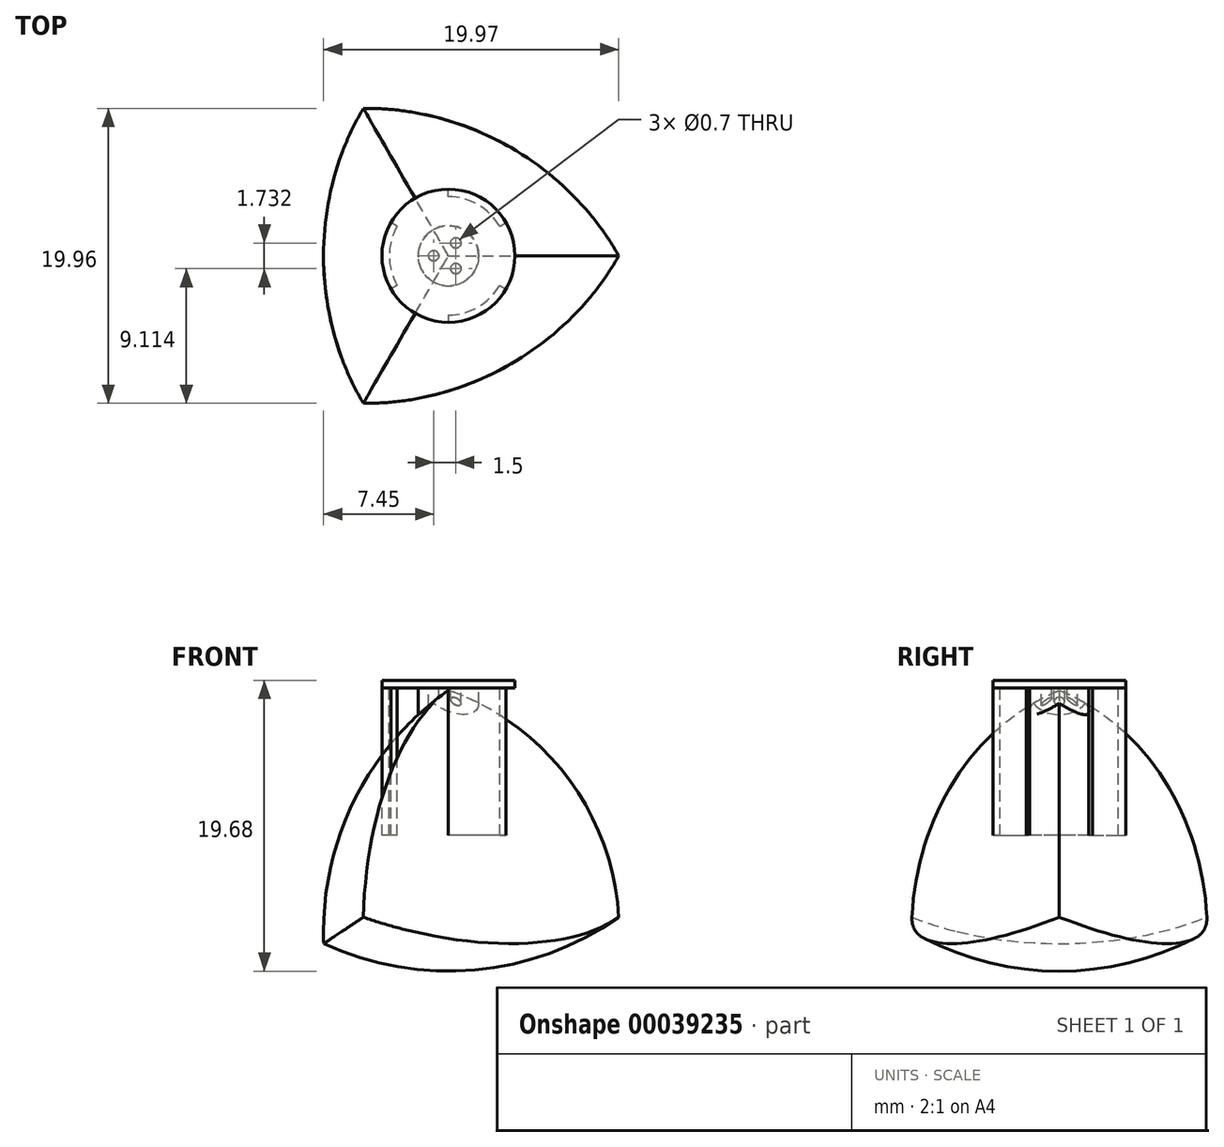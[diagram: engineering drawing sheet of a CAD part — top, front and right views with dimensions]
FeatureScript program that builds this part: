
annotation { "Feature Type Name" : "Feature", "Feature Type Description" : "" }
export const myFeature = defineFeature(function(context is Context, id is Id, definition is map)
    precondition{}
    {
        {
            var Q0;
            Q0=qCreatedBy(makeId("Top.planeOp"),FACE);
            var sketch = newSketch(context, id + "F0", { "sketchPlane" : qUnion([Q0])});
            skCircle(sketch, "E0", {"center": v(11.55, 0) * mm, "radius": 20 * mm});
            skCircle(sketch, "E1.1.0", {"center": v(-5.77, 10) * mm, "radius": 20 * mm});
            skCircle(sketch, "E1.2.0", {"center": v(-5.77, -10) * mm, "radius": 20 * mm});
            skPoint(sketch, "E1.center", {"position": v(0, 0) * mm});
            skLineSegment(sketch, "E2", {"start": v(31.55, 0) * mm, "end": v(-8.45, 0) * mm});
            skLineSegment(sketch, "E3", {"start": v(0, 0) * mm, "end": v(-5.77, -10) * mm});
            skLineSegment(sketch, "E4", {"start": v(-5.77, -10) * mm, "end": v(-15.77, -27.32) * mm});
            skLineSegment(sketch, "E5", {"start": v(0, 0) * mm, "end": v(4.23, 7.32) * mm});
            skLineSegment(sketch, "E6", {"start": v(-5.77, 10) * mm, "end": v(0, 0) * mm});
            skLineSegment(sketch, "E7", {"start": v(0, 0) * mm, "end": v(4.23, -7.32) * mm});
            skLineSegment(sketch, "E8", {"start": v(-5.77, 10) * mm, "end": v(-15.77, 27.32) * mm});
            skSolve(sketch);
        }
        {
            var Q0;
            {var subQ1=sQuery(id+"F0.wireOp",EDGE,"E2");var subQ3=sQuery(id+"F0.wireOp",EDGE,"E0");var subQ5=makeQuery(id+"F0.imprint","INTERSECT",VERTEX,{"disambiguationData":[OD(0.0)],"derivedFrom":[subQ3,subQ1]});Q0=makeQuery(id+"F0.imprint","IMPRINT",FACE,{"disambiguationData":[TD([[makeQuery(id+"F0.imprint","IMPRINT",EDGE,{"disambiguationData":[TD([[subQ5,-1.0]])],"derivedFrom":subQ3}),1.0]])]});}
            var Q1;
            {var subQ1=sQuery(id+"F0.wireOp",EDGE,"E0");var subQ4=sQuery(id+"F0.wireOp",EDGE,"E1.1.0");var subQ6=makeQuery(id+"F0.imprint","INTERSECT",VERTEX,{"derivedFrom":[subQ1,subQ4]});Q1=makeQuery(id+"F0.imprint","IMPRINT",FACE,{"disambiguationData":[TD([[makeQuery(id+"F0.imprint","IMPRINT",EDGE,{"disambiguationData":[TD([[subQ6,1.0]])],"derivedFrom":subQ4}),1.0]])]});}
            var Q2;
            {var subQ1=sQuery(id+"F0.wireOp",EDGE,"E5");Q2=makeQuery(id+"F0.imprint","IMPRINT",FACE,{"disambiguationData":[TD([[makeQuery(id+"F0.imprint","IMPRINT",EDGE,{"derivedFrom":subQ1}),1.0]])]});}
            var Q3;
            {var subQ0=sQuery(id+"F0.wireOp",EDGE,"E5");Q3=makeQuery(id+"F0.imprint","IMPRINT",FACE,{"disambiguationData":[TD([[makeQuery(id+"F0.imprint","IMPRINT",EDGE,{"derivedFrom":subQ0}),-1.0]])]});}
            var Q4;
            {var subQ0=sQuery(id+"F0.wireOp",EDGE,"E6");Q4=makeQuery(id+"F0.imprint","IMPRINT",FACE,{"disambiguationData":[TD([[makeQuery(id+"F0.imprint","IMPRINT",EDGE,{"derivedFrom":subQ0}),-1.0]])]});}
            var Q5;
            Q5=sQuery(id+"F0.wireOp",EDGE,"E2");
            revolve(context, id + "F1", {"entities" : qUnion([Q0, Q1, Q2, Q3, Q4]), "axis" : qUnion([Q5]), "revolveType" : RevolveType.FULL});
        }
        {
            var Q0;
            {var subQ1=sQuery(id+"F0.wireOp",EDGE,"E0");var subQ4=sQuery(id+"F0.wireOp",EDGE,"E1.1.0");var subQ6=makeQuery(id+"F0.imprint","INTERSECT",VERTEX,{"derivedFrom":[subQ1,subQ4]});Q0=makeQuery(id+"F0.imprint","IMPRINT",FACE,{"disambiguationData":[TD([[makeQuery(id+"F0.imprint","IMPRINT",EDGE,{"disambiguationData":[TD([[subQ6,1.0]])],"derivedFrom":subQ4}),1.0]])]});}
            var Q1;
            {var subQ0=sQuery(id+"F0.wireOp",EDGE,"E5");Q1=makeQuery(id+"F0.imprint","IMPRINT",FACE,{"disambiguationData":[TD([[makeQuery(id+"F0.imprint","IMPRINT",EDGE,{"derivedFrom":subQ0}),-1.0]])]});}
            var Q2;
            {var subQ1=sQuery(id+"F0.wireOp",EDGE,"E5");Q2=makeQuery(id+"F0.imprint","IMPRINT",FACE,{"disambiguationData":[TD([[makeQuery(id+"F0.imprint","IMPRINT",EDGE,{"derivedFrom":subQ1}),1.0]])]});}
            var Q3;
            {var subQ3=sQuery(id+"F0.wireOp",EDGE,"E7");Q3=makeQuery(id+"F0.imprint","IMPRINT",FACE,{"disambiguationData":[TD([[makeQuery(id+"F0.imprint","IMPRINT",EDGE,{"derivedFrom":subQ3}),1.0]])]});}
            var Q4;
            {var subQ0=sQuery(id+"F0.wireOp",EDGE,"E8");Q4=makeQuery(id+"F0.imprint","IMPRINT",FACE,{"disambiguationData":[TD([[makeQuery(id+"F0.imprint","IMPRINT",EDGE,{"derivedFrom":subQ0}),-1.0]])]});}
            var Q5;
            Q5=sQuery(id+"F0.wireOp",EDGE,"E8");
            revolve(context, id + "F2", {"entities" : qUnion([Q0, Q1, Q2, Q3, Q4]), "axis" : qUnion([Q5]), "revolveType" : RevolveType.FULL});
        }
        {
            var Q0;
            {var subQ3=sQuery(id+"F0.wireOp",EDGE,"E4");Q0=makeQuery(id+"F0.imprint","IMPRINT",FACE,{"disambiguationData":[TD([[makeQuery(id+"F0.imprint","IMPRINT",EDGE,{"derivedFrom":subQ3}),-1.0]])]});}
            var Q1;
            {var subQ3=sQuery(id+"F0.wireOp",EDGE,"E0");var subQ6=makeQuery(id+"F0.imprint","INTERSECT",VERTEX,{"disambiguationData":[OD(1.0)],"derivedFrom":[subQ3,sQuery(id+"F0.wireOp",EDGE,"E2")]});Q1=makeQuery(id+"F0.imprint","IMPRINT",FACE,{"disambiguationData":[TD([[makeQuery(id+"F0.imprint","IMPRINT",EDGE,{"disambiguationData":[TD([[subQ6,1.0]])],"derivedFrom":subQ3}),-1.0]])]});}
            var Q2;
            {var subQ0=sQuery(id+"F0.wireOp",EDGE,"E3");Q2=makeQuery(id+"F0.imprint","IMPRINT",FACE,{"disambiguationData":[TD([[makeQuery(id+"F0.imprint","IMPRINT",EDGE,{"derivedFrom":subQ0}),-1.0]])]});}
            var Q3;
            {var subQ0=sQuery(id+"F0.wireOp",EDGE,"E6");Q3=makeQuery(id+"F0.imprint","IMPRINT",FACE,{"disambiguationData":[TD([[makeQuery(id+"F0.imprint","IMPRINT",EDGE,{"derivedFrom":subQ0}),-1.0]])]});}
            var Q4;
            {var subQ1=sQuery(id+"F0.wireOp",EDGE,"E5");Q4=makeQuery(id+"F0.imprint","IMPRINT",FACE,{"disambiguationData":[TD([[makeQuery(id+"F0.imprint","IMPRINT",EDGE,{"derivedFrom":subQ1}),1.0]])]});}
            var Q5;
            Q5=sQuery(id+"F0.wireOp",EDGE,"E4");
            revolve(context, id + "F3", {"entities" : qUnion([Q0, Q1, Q2, Q3, Q4]), "axis" : qUnion([Q5]), "revolveType" : RevolveType.FULL});
        }
        {
            var Q0;
            Q0=qCreatedBy(makeId("Top.planeOp"),FACE);
            cPlane(context, id + "F4", {"entities" : qUnion([Q0]), "cplaneType" : CPlaneType.OFFSET, "offset" : 17.32 * mm, "width" : 150 * mm, "height" : 150 * mm});
        }
        {
            var Q0;
            Q0=qCreatedBy(id+"F4.planeOp",FACE);
            var sketch = newSketch(context, id + "F5", { "sketchPlane" : qUnion([Q0])});
            skCircle(sketch, "E9", {"center": v(0, 0) * mm, "radius": 20 * mm});
            skLineSegment(sketch, "E10", {"start": v(20, 0) * mm, "end": v(-20, 0) * mm});
            skSolve(sketch);
        }
        {
            var Q0;
            {var subQ0=sQuery(id+"F5.wireOp",EDGE,"E10");Q0=makeQuery(id+"F5.imprint","IMPRINT",FACE,{"disambiguationData":[TD([[makeQuery(id+"F5.imprint","IMPRINT",EDGE,{"derivedFrom":subQ0}),-1.0]])]});}
            var Q1;
            Q1=sQuery(id+"F5.wireOp",EDGE,"E10");
            revolve(context, id + "F6", {"entities" : qUnion([Q0]), "axis" : qUnion([Q1]), "revolveType" : RevolveType.FULL});
        }
        {
            var Q0;
            Q0=makeQuery(id+"F6.opRevolve","SWEPT_BODY",BODY,{"disambiguationData":[OSD([sQuery(id+"F5.wireOp",EDGE,"E9"),sQuery(id+"F5.wireOp",EDGE,"E10")])]});
            var Q1;
            Q1=makeQuery(id+"F1.opRevolve","SWEPT_BODY",BODY,{"disambiguationData":[OSD([sQuery(id+"F0.wireOp",EDGE,"E0"),sQuery(id+"F0.wireOp",EDGE,"E2")])]});
            var Q2;
            Q2=makeQuery(id+"F3.opRevolve","SWEPT_BODY",BODY,{"disambiguationData":[OSD([sQuery(id+"F0.wireOp",EDGE,"E1.2.0"),sQuery(id+"F0.wireOp",EDGE,"E3"),sQuery(id+"F0.wireOp",EDGE,"E4"),sQuery(id+"F0.wireOp",EDGE,"E5")])]});
            var Q3;
            Q3=makeQuery(id+"F2.opRevolve","SWEPT_BODY",BODY,{"disambiguationData":[OSD([sQuery(id+"F0.wireOp",EDGE,"E1.1.0"),sQuery(id+"F0.wireOp",EDGE,"E6"),sQuery(id+"F0.wireOp",EDGE,"E7"),sQuery(id+"F0.wireOp",EDGE,"E8")])]});
            booleanBodies(context, id + "F7", {"operationType" : BooleanOperationType.INTERSECTION, "tools" : qUnion([Q0, Q1, Q2, Q3])});
        }
        {
            var Q0;
            Q0=qCreatedBy(makeId("Top.planeOp"),FACE);
            var Q1;
            Q1 = qBodyType(qCreatedBy(id + "F9" ,EDGE), BodyType.WIRE);
            cPlane(context, id + "F8", {"entities" : qUnion([Q0, Q1]), "cplaneType" : CPlaneType.OFFSET, "offset" : 16.5 * mm, "width" : 150 * mm, "height" : 150 * mm});
        }
        {
            var Q0;
            Q0=qCreatedBy(id+"F8.planeOp",FACE);
            var sketch = newSketch(context, id + "F9", { "sketchPlane" : qUnion([Q0])});
            skCircle(sketch, "E11", {"center": v(0, 0) * mm, "radius": 2.04 * mm});
            skSolve(sketch);
        }
        {
            var Q0;
            Q0=makeQuery(id+"F9.imprint","IMPRINT",FACE,{"disambiguationData":[TD([[makeQuery(id+"F9.imprint","IMPRINT",EDGE,{"derivedFrom":sQuery(id+"F9.wireOp",EDGE,"E11")}),1.0]])]});
            extrude(context, id + "F10", {"entities" : qUnion([Q0]), "oppositeDirection" : true, "depth" : 10 * mm});
        }
        {
            var Q0;
            Q0=qCreatedBy(id+"F8.planeOp",FACE);
            var sketch = newSketch(context, id + "F11", { "sketchPlane" : qUnion([Q0])});
            skCircle(sketch, "E12", {"center": v(0, 0) * mm, "radius": 4 * mm});
            skCircle(sketch, "E13", {"center": v(0, 0) * mm, "radius": 4.5 * mm});
            skLineSegment(sketch, "E14", {"start": v(0, 0) * mm, "end": v(0, 4.5) * mm});
            skLineSegment(sketch, "E15", {"start": v(0, 0) * mm, "end": v(3.9, 2.25) * mm});
            skSolve(sketch);
        }
        {
            var Q0;
            {var subQ1=sQuery(id+"F11.wireOp",EDGE,"E12");var subQ5=sQuery(id+"F11.wireOp",EDGE,"E14");var subQ7=makeQuery(id+"F11.imprint","INTERSECT",VERTEX,{"derivedFrom":[subQ1,subQ5]});Q0=makeQuery(id+"F11.imprint","IMPRINT",FACE,{"disambiguationData":[TD([[makeQuery(id+"F11.imprint","IMPRINT",EDGE,{"disambiguationData":[TD([[subQ7,1.0]])],"derivedFrom":subQ1}),-1.0]])]});}
            extrude(context, id + "F12", {"entities" : qUnion([Q0]), "oppositeDirection" : true, "depth" : 10 * mm});
        }
        {
            var Q0;
            Q0=makeQuery(id+"F12.opExtrude","SWEPT_BODY",BODY,{"disambiguationData":[OSD([sQuery(id+"F11.wireOp",EDGE,"E12"),sQuery(id+"F11.wireOp",EDGE,"E13"),sQuery(id+"F11.wireOp",EDGE,"E14"),sQuery(id+"F11.wireOp",EDGE,"E15")])]});
            var Q1;
            Q1=makeQuery(id+"F10.opExtrude","CAP_EDGE",EDGE,{"disambiguationData":[OSD([sQuery(id+"F9.wireOp",EDGE,"E11")])],"isStart":true});
            circularPattern(context, id + "F13", {"entities" : qUnion([Q0]), "axis" : qUnion([Q1]), "angle" : 120 * degree, "instanceCount" : 3});
        }
        {
            var Q0;
            Q0=qCreatedBy(id+"F8.planeOp",FACE);
            var sketch = newSketch(context, id + "F14", { "sketchPlane" : qUnion([Q0])});
            skCircle(sketch, "E16", {"center": v(0, 0) * mm, "radius": 4.5 * mm});
            skSolve(sketch);
        }
        {
            var Q0;
            Q0=makeQuery(id+"F14.imprint","IMPRINT",FACE,{"disambiguationData":[TD([[makeQuery(id+"F14.imprint","IMPRINT",EDGE,{"derivedFrom":sQuery(id+"F14.wireOp",EDGE,"E16")}),1.0]])]});
            extrude(context, id + "F15", {"entities" : qUnion([Q0]), "depth" : 0.5 * mm});
        }
        {
            var Q0;
            Q0=makeQuery(id+"F10.opExtrude","CAP_FACE",FACE,{"disambiguationData":[OSD([sQuery(id+"F9.wireOp",EDGE,"E11")])],"isStart":true});
            var sketch = newSketch(context, id + "F16", { "sketchPlane" : qUnion([Q0])});
            skCircle(sketch, "E17", {"center": v(-1, 0) * mm, "radius": 0.35 * mm});
            skCircle(sketch, "E18.1.0", {"center": v(0.5, -0.87) * mm, "radius": 0.35 * mm});
            skCircle(sketch, "E18.2.0", {"center": v(0.5, 0.87) * mm, "radius": 0.35 * mm});
            skPoint(sketch, "E18.center", {"position": v(0, 0) * mm});
            skSolve(sketch);
        }
        {
            var Q0;
            Q0=makeQuery(id+"F16.imprint","IMPRINT",FACE,{"disambiguationData":[TD([[makeQuery(id+"F16.imprint","IMPRINT",EDGE,{"derivedFrom":sQuery(id+"F16.wireOp",EDGE,"E17")}),1.0]])]});
            var Q1;
            Q1=makeQuery(id+"F16.imprint","IMPRINT",FACE,{"disambiguationData":[TD([[makeQuery(id+"F16.imprint","IMPRINT",EDGE,{"derivedFrom":sQuery(id+"F16.wireOp",EDGE,"E18.1.0")}),1.0]])]});
            var Q2;
            Q2=makeQuery(id+"F16.imprint","IMPRINT",FACE,{"disambiguationData":[TD([[makeQuery(id+"F16.imprint","IMPRINT",EDGE,{"derivedFrom":sQuery(id+"F16.wireOp",EDGE,"E18.2.0")}),1.0]])]});
            extrude(context, id + "F17", {"entities" : qUnion([Q0, Q1, Q2]), "oppositeDirection" : true, "depth" : 25 * mm});
        }
        {
            var Q0;
            Q0=makeQuery(id+"F17.opExtrude","SWEPT_BODY",BODY,{"disambiguationData":[OSD([sQuery(id+"F16.wireOp",EDGE,"E17")])]});
            var Q1;
            Q1=makeQuery(id+"F17.opExtrude","SWEPT_BODY",BODY,{"disambiguationData":[OSD([sQuery(id+"F16.wireOp",EDGE,"E18.1.0")])]});
            var Q2;
            Q2=makeQuery(id+"F17.opExtrude","SWEPT_BODY",BODY,{"disambiguationData":[OSD([sQuery(id+"F16.wireOp",EDGE,"E18.2.0")])]});
            var Q3;
            Q3=makeQuery(id+"F10.opExtrude","SWEPT_BODY",BODY,{"disambiguationData":[OSD([sQuery(id+"F9.wireOp",EDGE,"E11")])]});
            booleanBodies(context, id + "F18", {"operationType" : BooleanOperationType.SUBTRACTION, "tools" : qUnion([Q0, Q1, Q2]), "targets" : qUnion([Q3])});
        }
        {
            var Q0;
            Q0=makeQuery(id+"F7.opBoolean","INTERSECT",BODY,{"derivedFrom":[makeQuery(id+"F1.opRevolve","SWEPT_BODY",BODY,{"disambiguationData":[OSD([sQuery(id+"F0.wireOp",EDGE,"E0"),sQuery(id+"F0.wireOp",EDGE,"E2")])]}),makeQuery(id+"F2.opRevolve","SWEPT_BODY",BODY,{"disambiguationData":[OSD([sQuery(id+"F0.wireOp",EDGE,"E1.1.0"),sQuery(id+"F0.wireOp",EDGE,"E6"),sQuery(id+"F0.wireOp",EDGE,"E7"),sQuery(id+"F0.wireOp",EDGE,"E8")])]}),makeQuery(id+"F3.opRevolve","SWEPT_BODY",BODY,{"disambiguationData":[OSD([sQuery(id+"F0.wireOp",EDGE,"E1.2.0"),sQuery(id+"F0.wireOp",EDGE,"E3"),sQuery(id+"F0.wireOp",EDGE,"E4"),sQuery(id+"F0.wireOp",EDGE,"E5")])]}),makeQuery(id+"F6.opRevolve","SWEPT_BODY",BODY,{"disambiguationData":[OSD([sQuery(id+"F5.wireOp",EDGE,"E9"),sQuery(id+"F5.wireOp",EDGE,"E10")])]})]});
            var Q1;
            Q1=makeQuery(id+"F10.opExtrude","SWEPT_BODY",BODY,{"disambiguationData":[OSD([sQuery(id+"F9.wireOp",EDGE,"E11")])]});
            booleanBodies(context, id + "F19", {"operationType" : BooleanOperationType.SUBTRACTION, "tools" : qUnion([Q0]), "targets" : qUnion([Q1]), "keepTools" : true});
        }
    });
